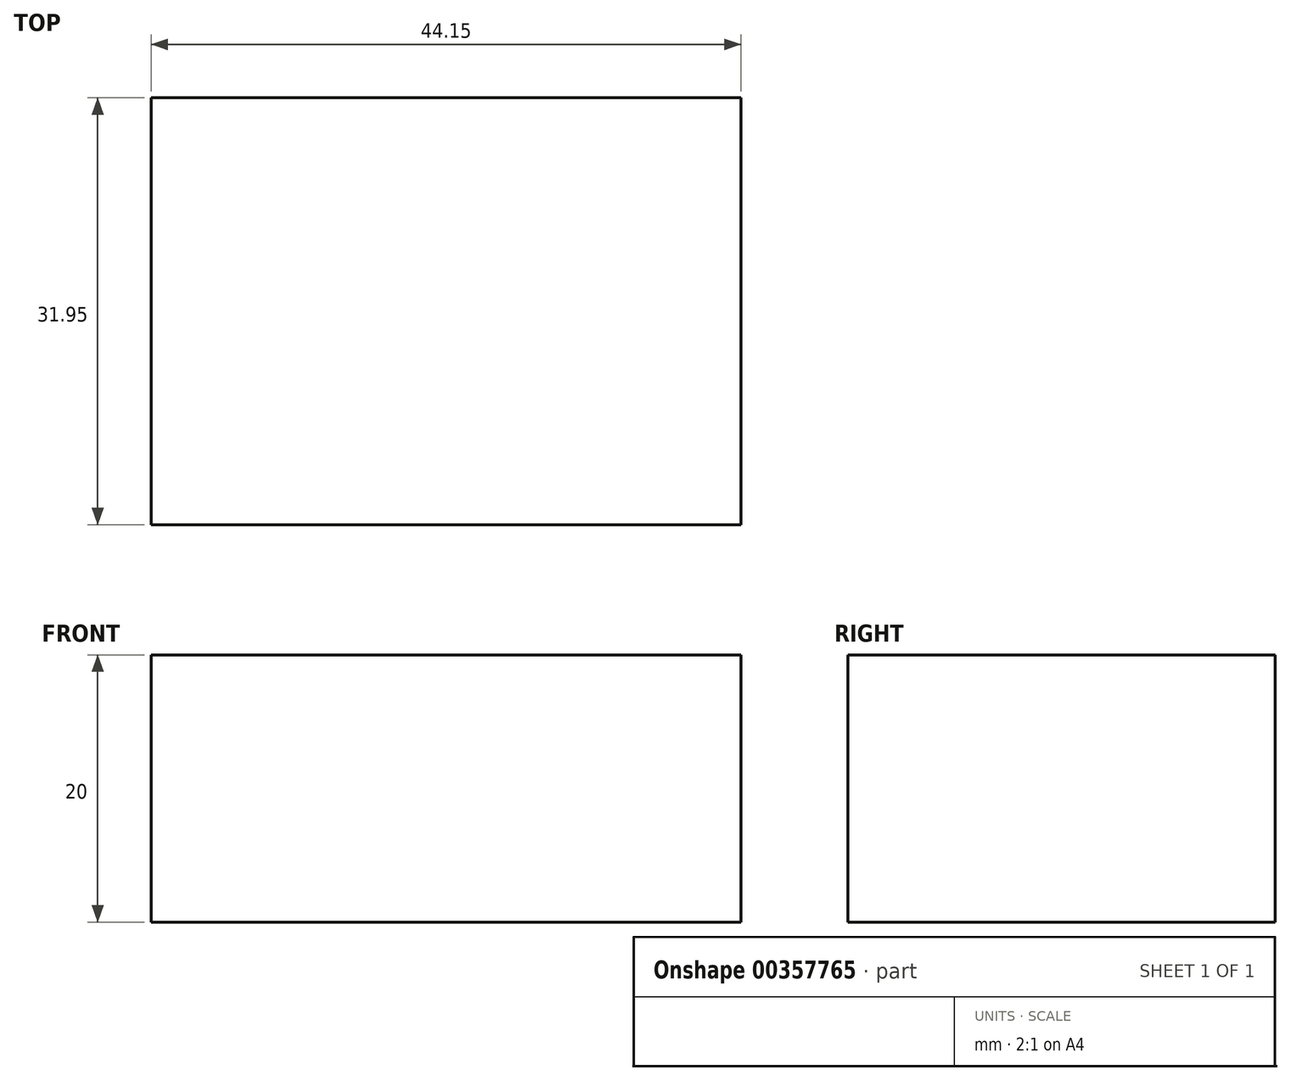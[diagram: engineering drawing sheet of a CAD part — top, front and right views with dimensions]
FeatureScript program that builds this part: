
annotation { "Feature Type Name" : "Feature", "Feature Type Description" : "" }
export const myFeature = defineFeature(function(context is Context, id is Id, definition is map)
    precondition{}
    {
        {
            var Q0;
            Q0=qCreatedBy(makeId("Top.planeOp"),FACE);
            var sketch = newSketch(context, id + "F0", { "sketchPlane" : qUnion([Q0])});
            skLineSegment(sketch, "E0.bottom", {"start": v(0, 0) * mm, "end": v(44.15, 0) * mm});
            skLineSegment(sketch, "E0.top", {"start": v(0, 31.95) * mm, "end": v(44.15, 31.95) * mm});
            skLineSegment(sketch, "E0.left", {"start": v(0, 0) * mm, "end": v(0, 31.95) * mm});
            skLineSegment(sketch, "E0.right", {"start": v(44.15, 0) * mm, "end": v(44.15, 31.95) * mm});
            skSolve(sketch);
        }
        {
            var Q0;
            Q0=makeQuery(id+"F0.imprint","IMPRINT",FACE,{"disambiguationData":[TD([[makeQuery(id+"F0.imprint","IMPRINT",EDGE,{"derivedFrom":sQuery(id+"F0.wireOp",EDGE,"E0.bottom")}),1.0]])]});
            extrude(context, id + "F1", {"entities" : qUnion([Q0]), "depth" : 20 * mm});
        }
    });
